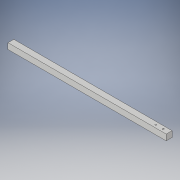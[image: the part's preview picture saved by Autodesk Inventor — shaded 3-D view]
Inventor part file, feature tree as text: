
AUTODESK INVENTOR PART (.ipt)
format: ipt  version: 2017 (Build 210142000, 142)  size: 107,520 bytes
history: native  units: in
note: dims shown in document units (in); Inventor stores cm internally (conversion verified against a paired STEP export)
features: extrude x2, sketch x2, plane x1
ambient origin geometry x8: Origin, YZ Plane, XZ Plane, XY Plane, X Axis, Y Axis, Z Axis, Center Point
bodies: Solid1 (feature_tree)
feature tree (5):
  plane  "Work Plane1"
  extrude  "Extrusion1"  Depth=13.5in
  extrude  "Extrusion2"  Depth=0.5in TaperAngle=0.0deg
  sketch  "Sketch1"  dims[d0=0.125in d1=13.5in]
  sketch  "Sketch2"  dims[d2=0.5in d3=0.5in d4=0.0in d5=0.25in d6=0.125in d7=0.5in d8=0.125in d9=0.25in d10=0.63in d11=0.01in d12=0.0in]
